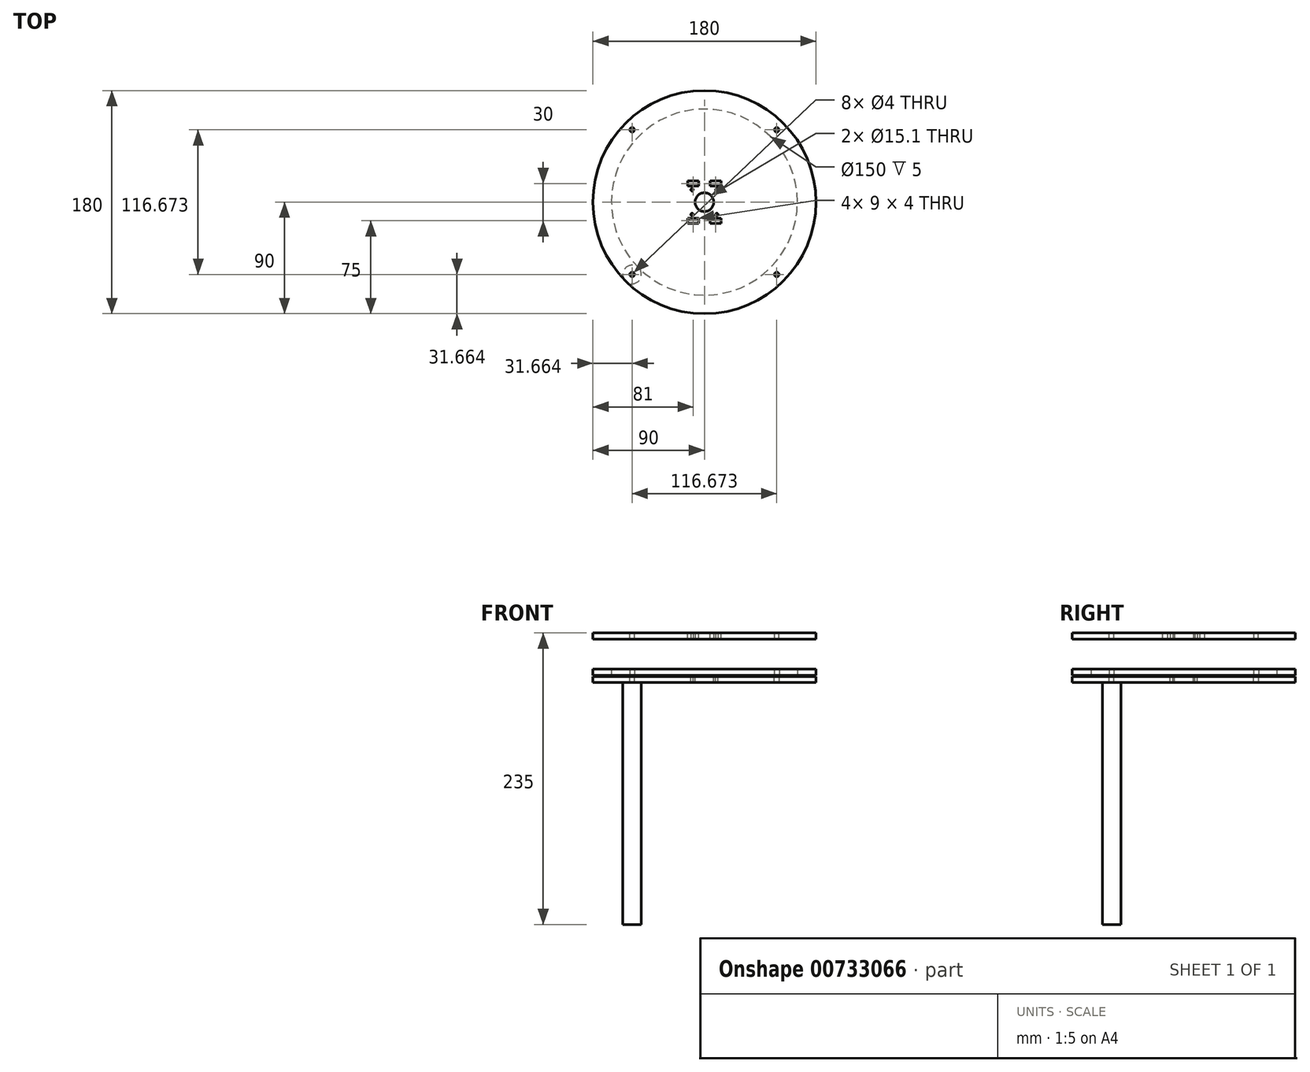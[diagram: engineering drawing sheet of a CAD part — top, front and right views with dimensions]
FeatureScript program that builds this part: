
annotation { "Feature Type Name" : "Feature", "Feature Type Description" : "" }
export const myFeature = defineFeature(function(context is Context, id is Id, definition is map)
    precondition{}
    {
        {
            var Q0;
            Q0=qCreatedBy(makeId("Top.planeOp"),FACE);
            var sketch = newSketch(context, id + "F0", { "sketchPlane" : qUnion([Q0])});
            skCircle(sketch, "E0", {"center": v(0, 0) * mm, "radius": 90 * mm});
            skCircle(sketch, "E1", {"center": v(0, 0) * mm, "radius": 75 * mm});
            skLineSegment(sketch, "E2", {"start": v(-75, 0) * mm, "end": v(-90, 0) * mm, "construction": true});
            skCircle(sketch, "E3", {"center": v(0, 0) * mm, "radius": 82.5 * mm, "construction": true});
            skPoint(sketch, "E4", {"position": v(-82.5, 0) * mm});
            skLineSegment(sketch, "E5", {"start": v(0, 0) * mm, "end": v(-58.34, 58.34) * mm, "construction": true});
            skCircle(sketch, "E6", {"center": v(-58.34, 58.34) * mm, "radius": 2 * mm});
            skCircle(sketch, "E7.MirrorC", {"center": v(58.34, 58.34) * mm, "radius": 2 * mm});
            skCircle(sketch, "E8.MirrorC", {"center": v(-58.34, -58.34) * mm, "radius": 2 * mm});
            skCircle(sketch, "E9.MirrorC", {"center": v(58.34, -58.34) * mm, "radius": 2 * mm});
            skSolve(sketch);
        }
        {
            var Q0;
            Q0=qSketchRegion(id+"F0",true);
            extrude(context, id + "F1", {"entities" : qUnion([Q0]), "depth" : 5 * mm, "offsetDistance" : 25 * mm});
        }
        {
            var Q0;
            Q0=makeQuery(id+"F1.opExtrude","CAP_FACE",FACE,{"disambiguationData":[OSD([sQuery(id+"F0.wireOp",EDGE,"E0"),sQuery(id+"F0.wireOp",EDGE,"E1"),sQuery(id+"F0.wireOp",EDGE,"E6"),sQuery(id+"F0.wireOp",EDGE,"E7.MirrorC"),sQuery(id+"F0.wireOp",EDGE,"E8.MirrorC"),sQuery(id+"F0.wireOp",EDGE,"E9.MirrorC")])],"isStart":true});
            cPlane(context, id + "F2", {"entities" : qUnion([Q0]), "cplaneType" : CPlaneType.OFFSET, "offset" : 1 * mm, "width" : 150 * mm, "height" : 150 * mm});
        }
        {
            var Q0;
            Q0=qCreatedBy(id+"F2.planeOp",FACE);
            var sketch = newSketch(context, id + "F3", { "sketchPlane" : qUnion([Q0])});
            skCircle(sketch, "E10.0", {"center": v(0, 0) * mm, "radius": 90 * mm});
            skCircle(sketch, "E11.0", {"center": v(-58.34, 58.34) * mm, "radius": 2 * mm});
            skCircle(sketch, "E12.0", {"center": v(58.34, 58.34) * mm, "radius": 2 * mm});
            skCircle(sketch, "E13.0", {"center": v(58.34, -58.34) * mm, "radius": 2 * mm});
            skCircle(sketch, "E14.0", {"center": v(-58.34, -58.34) * mm, "radius": 2 * mm});
            skCircle(sketch, "E15", {"center": v(0, 0) * mm, "radius": 7.55 * mm});
            skSolve(sketch);
        }
        {
            var Q0;
            Q0=qSketchRegion(id+"F3",true);
            extrude(context, id + "F4", {"entities" : qUnion([Q0]), "depth" : 5 * mm, "offsetDistance" : 25 * mm});
        }
        {
            var Q0;
            Q0=makeQuery(id+"F4.opExtrude","CAP_FACE",FACE,{"disambiguationData":[OSD([sQuery(id+"F3.wireOp",EDGE,"E10.0"),sQuery(id+"F3.wireOp",EDGE,"E11.0"),sQuery(id+"F3.wireOp",EDGE,"E12.0"),sQuery(id+"F3.wireOp",EDGE,"E13.0"),sQuery(id+"F3.wireOp",EDGE,"E14.0"),sQuery(id+"F3.wireOp",EDGE,"E15")])],"isStart":true});
            var sketch = newSketch(context, id + "F5", { "sketchPlane" : qUnion([Q0])});
            skLineSegment(sketch, "E16.bottom", {"start": v(-10, 10) * mm, "end": v(10, 10) * mm, "construction": true});
            skLineSegment(sketch, "E16.top", {"start": v(-10, -10) * mm, "end": v(10, -10) * mm, "construction": true});
            skLineSegment(sketch, "E16.left", {"start": v(-10, 10) * mm, "end": v(-10, -10) * mm, "construction": true});
            skLineSegment(sketch, "E16.right", {"start": v(10, 10) * mm, "end": v(10, -10) * mm, "construction": true});
            skPoint(sketch, "E16.middle", {"position": v(0, 0) * mm});
            skCircle(sketch, "E17", {"center": v(-10, 10) * mm, "radius": 1 * mm});
            skCircle(sketch, "E18.MirrorC", {"center": v(10, 10) * mm, "radius": 1 * mm});
            skCircle(sketch, "E19.MirrorC", {"center": v(-10, -10) * mm, "radius": 1 * mm});
            skCircle(sketch, "E20.MirrorC", {"center": v(10, -10) * mm, "radius": 1 * mm});
            skSolve(sketch);
        }
        {
            var Q0;
            Q0=qSketchRegion(id+"F5",true);
            extrude(context, id + "F6", {"entities" : qUnion([Q0]), "operationType" : NewBodyOperationType.REMOVE, "endBound" : BoundingType.UP_TO_NEXT, "oppositeDirection" : true, "depth" : 25 * mm, "offsetDistance" : 25 * mm});
        }
        {
            var Q0;
            Q0=makeQuery(id+"F4.opExtrude","CAP_FACE",FACE,{"disambiguationData":[OSD([sQuery(id+"F3.wireOp",EDGE,"E10.0"),sQuery(id+"F3.wireOp",EDGE,"E11.0"),sQuery(id+"F3.wireOp",EDGE,"E12.0"),sQuery(id+"F3.wireOp",EDGE,"E13.0"),sQuery(id+"F3.wireOp",EDGE,"E14.0"),sQuery(id+"F3.wireOp",EDGE,"E15")])],"isStart":false});
            var sketch = newSketch(context, id + "F7", { "sketchPlane" : qUnion([Q0])});
            skPoint(sketch, "E21.center", {"position": v(0, 0) * mm});
            skCircle(sketch, "E22", {"center": v(-58.34, 58.34) * mm, "radius": 7.5 * mm});
            skSolve(sketch);
        }
        {
            var Q0;
            Q0=qSketchRegion(id+"F7",true);
            extrude(context, id + "F8", {"entities" : qUnion([Q0]), "depth" : 195 * mm, "offsetDistance" : 25 * mm});
        }
        {
            var Q0;
            Q0=makeQuery(id+"F4.opExtrude","CAP_FACE",FACE,{"disambiguationData":[OSD([sQuery(id+"F3.wireOp",EDGE,"E10.0"),sQuery(id+"F3.wireOp",EDGE,"E11.0"),sQuery(id+"F3.wireOp",EDGE,"E12.0"),sQuery(id+"F3.wireOp",EDGE,"E13.0"),sQuery(id+"F3.wireOp",EDGE,"E14.0"),sQuery(id+"F3.wireOp",EDGE,"E15")])],"isStart":false});
            cPlane(context, id + "F9", {"entities" : qUnion([Q0]), "cplaneType" : CPlaneType.OFFSET, "offset" : 20 * mm, "oppositeDirection" : true, "width" : 150 * mm, "height" : 150 * mm});
        }
        {
            var Q0;
            Q0=makeQuery(id+"F4.opExtrude","SWEPT_BODY",BODY,{"disambiguationData":[OSD([sQuery(id+"F3.wireOp",EDGE,"E10.0"),sQuery(id+"F3.wireOp",EDGE,"E11.0"),sQuery(id+"F3.wireOp",EDGE,"E12.0"),sQuery(id+"F3.wireOp",EDGE,"E13.0"),sQuery(id+"F3.wireOp",EDGE,"E14.0"),sQuery(id+"F3.wireOp",EDGE,"E15")])]});
            var Q1;
            Q1=qCreatedBy(id+"F9.planeOp",FACE);
            mirror(context, id + "F10", {"entities" : qUnion([Q0]), "mirrorPlane" : qUnion([Q1])});
        }
        {
            var Q0;
            Q0=makeQuery(id+"F10.opPattern","COPY",FACE,{"derivedFrom":makeQuery(id+"F4.opExtrude","CAP_FACE",FACE,{"disambiguationData":[OSD([sQuery(id+"F3.wireOp",EDGE,"E10.0"),sQuery(id+"F3.wireOp",EDGE,"E11.0"),sQuery(id+"F3.wireOp",EDGE,"E12.0"),sQuery(id+"F3.wireOp",EDGE,"E13.0"),sQuery(id+"F3.wireOp",EDGE,"E14.0"),sQuery(id+"F3.wireOp",EDGE,"E15")])],"isStart":false}),"instanceName":"1"});
            var sketch = newSketch(context, id + "F11", { "sketchPlane" : qUnion([Q0])});
            skLineSegment(sketch, "E23.bottom", {"start": v(13, -13) * mm, "end": v(-13, -13) * mm, "construction": true});
            skLineSegment(sketch, "E23.top", {"start": v(13, -17) * mm, "end": v(-13, -17) * mm, "construction": true});
            skLineSegment(sketch, "E23.left", {"start": v(13, -13) * mm, "end": v(13, -17) * mm, "construction": true});
            skLineSegment(sketch, "E23.right", {"start": v(-13, -13) * mm, "end": v(-13, -17) * mm, "construction": true});
            skPoint(sketch, "E23.middle", {"position": v(0, -15) * mm});
            skLineSegment(sketch, "E24", {"start": v(5, -13) * mm, "end": v(5, -17) * mm, "construction": true});
            skLineSegment(sketch, "E25.MirrorCS", {"start": v(-5, -13) * mm, "end": v(-5, -17) * mm, "construction": true});
            skLineSegment(sketch, "E26", {"start": v(5, -13) * mm, "end": v(13, -17) * mm, "construction": true});
            skPoint(sketch, "E27", {"position": v(9, -15) * mm});
            skLineSegment(sketch, "E28.bottom", {"start": v(4.5, -13) * mm, "end": v(13.5, -13) * mm});
            skLineSegment(sketch, "E28.top", {"start": v(4.5, -17) * mm, "end": v(13.5, -17) * mm});
            skLineSegment(sketch, "E28.left", {"start": v(4.5, -13) * mm, "end": v(4.5, -17) * mm});
            skLineSegment(sketch, "E28.right", {"start": v(13.5, -13) * mm, "end": v(13.5, -17) * mm});
            skLineSegment(sketch, "E29.MirrorCS", {"start": v(-4.5, -13) * mm, "end": v(-4.5, -17) * mm});
            skLineSegment(sketch, "E30.MirrorCS", {"start": v(-4.5, -13) * mm, "end": v(-13.5, -13) * mm});
            skLineSegment(sketch, "E31.MirrorCS", {"start": v(-13.5, -13) * mm, "end": v(-13.5, -17) * mm});
            skLineSegment(sketch, "E32.MirrorCS", {"start": v(-4.5, -17) * mm, "end": v(-13.5, -17) * mm});
            skLineSegment(sketch, "E33.MirrorCS", {"start": v(-13.5, 13) * mm, "end": v(-13.5, 17) * mm});
            skLineSegment(sketch, "E34.MirrorCS", {"start": v(-4.5, 13) * mm, "end": v(-13.5, 13) * mm});
            skLineSegment(sketch, "E35.MirrorCS", {"start": v(-4.5, 13) * mm, "end": v(-4.5, 17) * mm});
            skLineSegment(sketch, "E36.MirrorCS", {"start": v(-4.5, 17) * mm, "end": v(-13.5, 17) * mm});
            skLineSegment(sketch, "E37.MirrorCS", {"start": v(4.5, 13) * mm, "end": v(4.5, 17) * mm});
            skLineSegment(sketch, "E38.MirrorCS", {"start": v(4.5, 13) * mm, "end": v(13.5, 13) * mm});
            skLineSegment(sketch, "E39.MirrorCS", {"start": v(13.5, 13) * mm, "end": v(13.5, 17) * mm});
            skLineSegment(sketch, "E40.MirrorCS", {"start": v(4.5, 17) * mm, "end": v(13.5, 17) * mm});
            skSolve(sketch);
        }
        {
            var Q0;
            Q0=qSketchRegion(id+"F11",true);
            extrude(context, id + "F12", {"entities" : qUnion([Q0]), "operationType" : NewBodyOperationType.REMOVE, "endBound" : BoundingType.UP_TO_NEXT, "oppositeDirection" : true, "depth" : 25 * mm, "offsetDistance" : 25 * mm});
        }
        {
            var Q0;
            Q0=makeQuery(id+"F10.opPattern","COPY",FACE,{"derivedFrom":makeQuery(id+"F4.opExtrude","CAP_FACE",FACE,{"disambiguationData":[OSD([sQuery(id+"F3.wireOp",EDGE,"E10.0"),sQuery(id+"F3.wireOp",EDGE,"E11.0"),sQuery(id+"F3.wireOp",EDGE,"E12.0"),sQuery(id+"F3.wireOp",EDGE,"E13.0"),sQuery(id+"F3.wireOp",EDGE,"E14.0"),sQuery(id+"F3.wireOp",EDGE,"E15")])],"isStart":false}),"instanceName":"1"});
            var sketch = newSketch(context, id + "F13", { "sketchPlane" : qUnion([Q0])});
            skCircle(sketch, "E41", {"center": v(-58.34, 58.34) * mm, "radius": 1.85 * mm});
            skCircle(sketch, "E42.0", {"center": v(-58.34, 58.34) * mm, "radius": 2 * mm});
            skCircle(sketch, "E43.1.0", {"center": v(-58.34, -58.34) * mm, "radius": 1.85 * mm});
            skCircle(sketch, "E43.1.1", {"center": v(-58.34, -58.34) * mm, "radius": 2 * mm});
            skCircle(sketch, "E43.2.0", {"center": v(58.34, -58.34) * mm, "radius": 1.85 * mm});
            skCircle(sketch, "E43.2.1", {"center": v(58.34, -58.34) * mm, "radius": 2 * mm});
            skCircle(sketch, "E43.3.0", {"center": v(58.34, 58.34) * mm, "radius": 1.85 * mm});
            skCircle(sketch, "E43.3.1", {"center": v(58.34, 58.34) * mm, "radius": 2 * mm});
            skPoint(sketch, "E43.center", {"position": v(0, 0) * mm});
            skSolve(sketch);
        }
        {
            var Q0;
            Q0=qSketchRegion(id+"F13",true);
            var Q1;
            Q1=makeQuery(id+"F10.opPattern","COPY",FACE,{"derivedFrom":makeQuery(id+"F4.opExtrude","CAP_FACE",FACE,{"disambiguationData":[OSD([sQuery(id+"F3.wireOp",EDGE,"E10.0"),sQuery(id+"F3.wireOp",EDGE,"E11.0"),sQuery(id+"F3.wireOp",EDGE,"E12.0"),sQuery(id+"F3.wireOp",EDGE,"E13.0"),sQuery(id+"F3.wireOp",EDGE,"E14.0"),sQuery(id+"F3.wireOp",EDGE,"E15")])],"isStart":true}),"instanceName":"1"});
            extrude(context, id + "F14", {"entities" : qUnion([Q0]), "operationType" : NewBodyOperationType.ADD, "endBound" : BoundingType.UP_TO_SURFACE, "oppositeDirection" : true, "depth" : 25 * mm, "endBoundEntityFace" : qUnion([Q1]), "offsetDistance" : 25 * mm});
        }
    });
